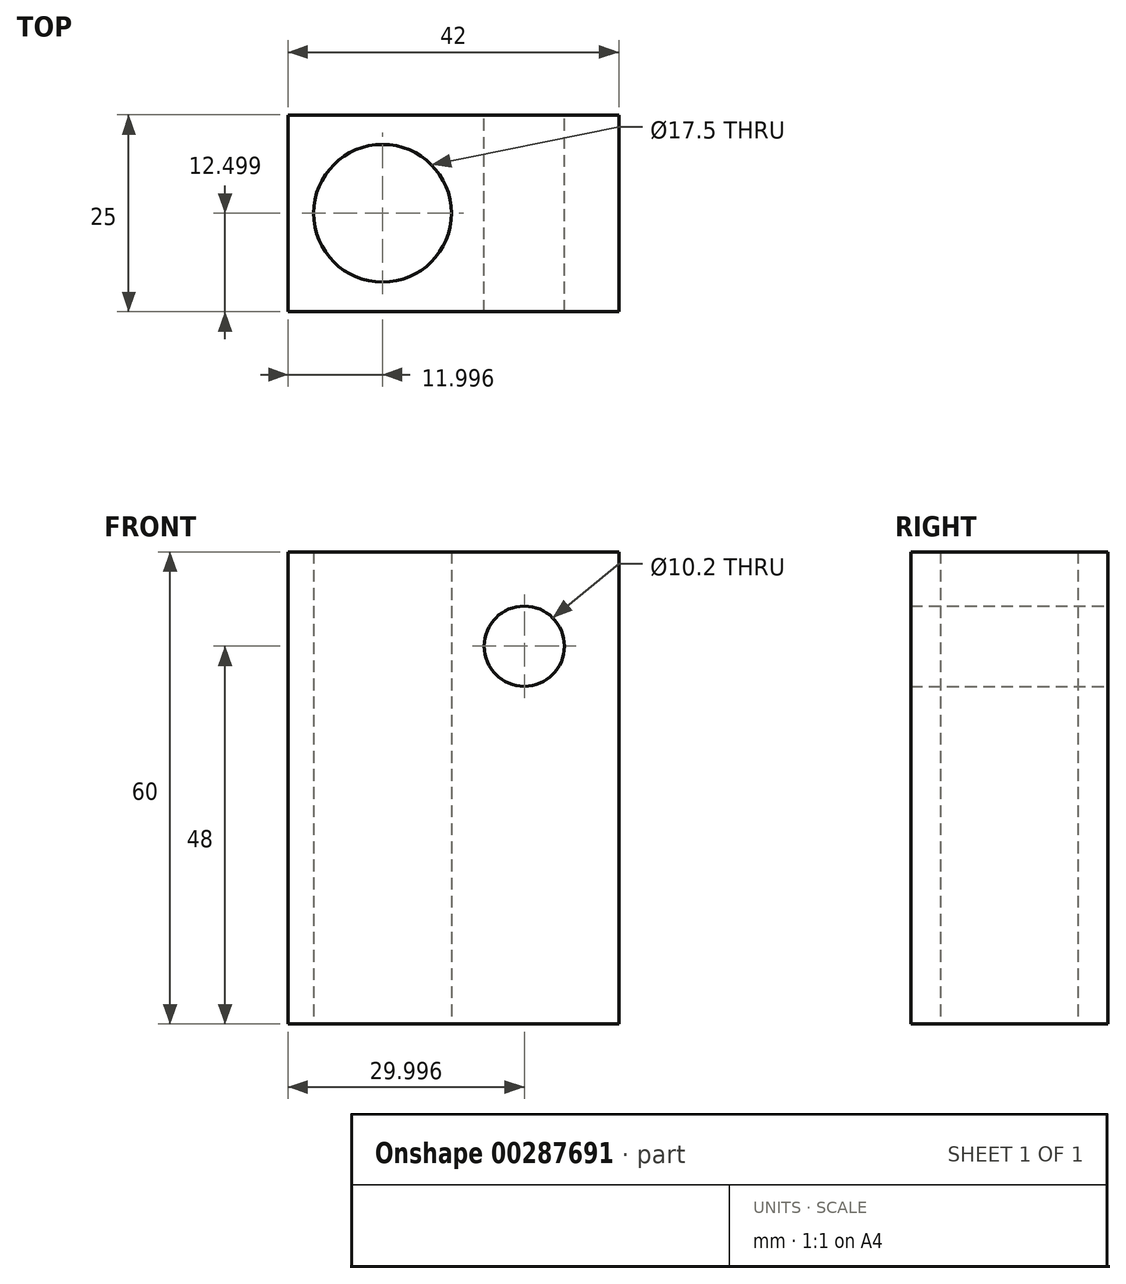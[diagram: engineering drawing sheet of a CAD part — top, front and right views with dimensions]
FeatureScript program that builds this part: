
annotation { "Feature Type Name" : "Feature", "Feature Type Description" : "" }
export const myFeature = defineFeature(function(context is Context, id is Id, definition is map)
    precondition{}
    {
        {
            var Q0;
            Q0=qCreatedBy(makeId("Top.planeOp"),FACE);
            var sketch = newSketch(context, id + "F0", { "sketchPlane" : qUnion([Q0])});
            skLineSegment(sketch, "E0", {"start": v(11.62, -31.21) * mm, "end": v(11.62, -6.21) * mm});
            skLineSegment(sketch, "E1", {"start": v(-30.38, -6.21) * mm, "end": v(-30.38, -18.71) * mm});
            skLineSegment(sketch, "E2", {"start": v(-30.38, -18.71) * mm, "end": v(-30.38, -31.21) * mm});
            skLineSegment(sketch, "E3", {"start": v(-30.38, -6.21) * mm, "end": v(-18.38, -6.21) * mm});
            skLineSegment(sketch, "E4", {"start": v(-18.38, -6.21) * mm, "end": v(11.62, -6.21) * mm});
            skLineSegment(sketch, "E5", {"start": v(-30.38, -31.21) * mm, "end": v(-5.38, -31.21) * mm});
            skLineSegment(sketch, "E6", {"start": v(-5.38, -31.21) * mm, "end": v(-5.38, -6.21) * mm, "construction": true});
            skPoint(sketch, "E7", {"position": v(-18.38, -18.71) * mm});
            skCircle(sketch, "E8", {"center": v(-18.38, -18.71) * mm, "radius": 8.75 * mm});
            skCircle(sketch, "E9", {"center": v(-18.38, -18.71) * mm, "radius": 5.1 * mm});
            skPoint(sketch, "E10.startSnap0", {"position": v(-3.38, -6.21) * mm});
            skPoint(sketch, "E10.start.orphan", {"position": v(0, -6.21) * mm});
            skLineSegment(sketch, "E11", {"start": v(-5.38, -31.21) * mm, "end": v(11.62, -31.21) * mm});
            skSolve(sketch);
        }
        {
            var Q0;
            Q0=makeQuery(id+"F0.imprint","IMPRINT",FACE,{"disambiguationData":[TD([[makeQuery(id+"F0.imprint","IMPRINT",EDGE,{"derivedFrom":sQuery(id+"F0.wireOp",EDGE,"E0")}),1.0]])]});
            extrude(context, id + "F1", {"entities" : qUnion([Q0]), "depth" : 60 * mm});
        }
        {
            var Q0;
            Q0=makeQuery(id+"F1.opExtrude","SWEPT_FACE",FACE,{"disambiguationData":[OSD([sQuery(id+"F0.wireOp",EDGE,"E3"),sQuery(id+"F0.wireOp",EDGE,"E4")])]});
            var sketch = newSketch(context, id + "F2", { "sketchPlane" : qUnion([Q0])});
            skPoint(sketch, "E12", {"position": v(0.38, 48) * mm});
            skCircle(sketch, "E13", {"center": v(0.38, 48) * mm, "radius": 5.1 * mm});
            skSolve(sketch);
        }
        {
            var Q0;
            Q0=sQuery(id+"F2.wireOp",VERTEX,"E12");
            var Q1;
            Q1=makeQuery(id+"F1.opExtrude","SWEPT_BODY",BODY,{"disambiguationData":[OSD([sQuery(id+"F0.wireOp",EDGE,"E0"),sQuery(id+"F0.wireOp",EDGE,"E1"),sQuery(id+"F0.wireOp",EDGE,"E2"),sQuery(id+"F0.wireOp",EDGE,"E3"),sQuery(id+"F0.wireOp",EDGE,"E4"),sQuery(id+"F0.wireOp",EDGE,"E5"),sQuery(id+"F0.wireOp",EDGE,"E8"),sQuery(id+"F0.wireOp",EDGE,"E11")])]});
            hole(context, id + "F3", {"style" : HoleStyle.SIMPLE, "endStyle" : HoleEndStyle.BLIND, "holeDiameter" : 10.2 * mm, "holeDepth" : 25 * mm, "tappedDepth" : 12 * mm, "tapClearance" : 3, "locations" : qUnion([Q0]), "scope" : qUnion([Q1])});
        }
    });
